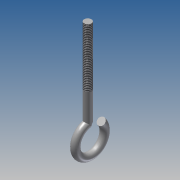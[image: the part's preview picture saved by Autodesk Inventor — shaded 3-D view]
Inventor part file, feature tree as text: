
AUTODESK INVENTOR PART (.ipt)
format: ipt  version: 2014 SP1 (Build 180222100, 222)  size: 224,768 bytes
history: native  units: in
note: dims shown in document units (in); Inventor stores cm internally (conversion verified against a paired STEP export)
features: sketch x3, plane x2, fillet x2, extrude x1, revolve x1, thread x1
ambient origin geometry x8: Origin, YZ Plane, XZ Plane, XY Plane, X Axis, Y Axis, Z Axis, Center Point
bodies: Solid1 (feature_tree)
feature tree (10):
  extrude  "Extrusion1"  Depth=1.5in TaperAngle=0.0deg
  sketch  "Sketch2"  dims[d15=-0.1in d17=0.125in d18=0.25in d19=2.1301in d20=0.125in]
  plane  "Work Plane1"
  plane  "Work Plane2"
  revolve  "Revolution1"  [1 undecoded]
  thread  "Thread5"  [1 undecoded]
  fillet  "Fillet1"  Radius=2.1301in
  fillet  "Fillet2"  Radius=0.125in
  sketch  "Sketch1"  dims[d0=0.125in d2=1.5in d3=0.0in]
  sketch  "Sketch5"  dims[d21=1.0in d22=0.0in d23=0.05in d24=0.03in]
note: 2 required parameter values undecoded (feature->parameter linkage not recoverable at this tier; creation-order binding heuristic only, values carry confidence <= 0.55)